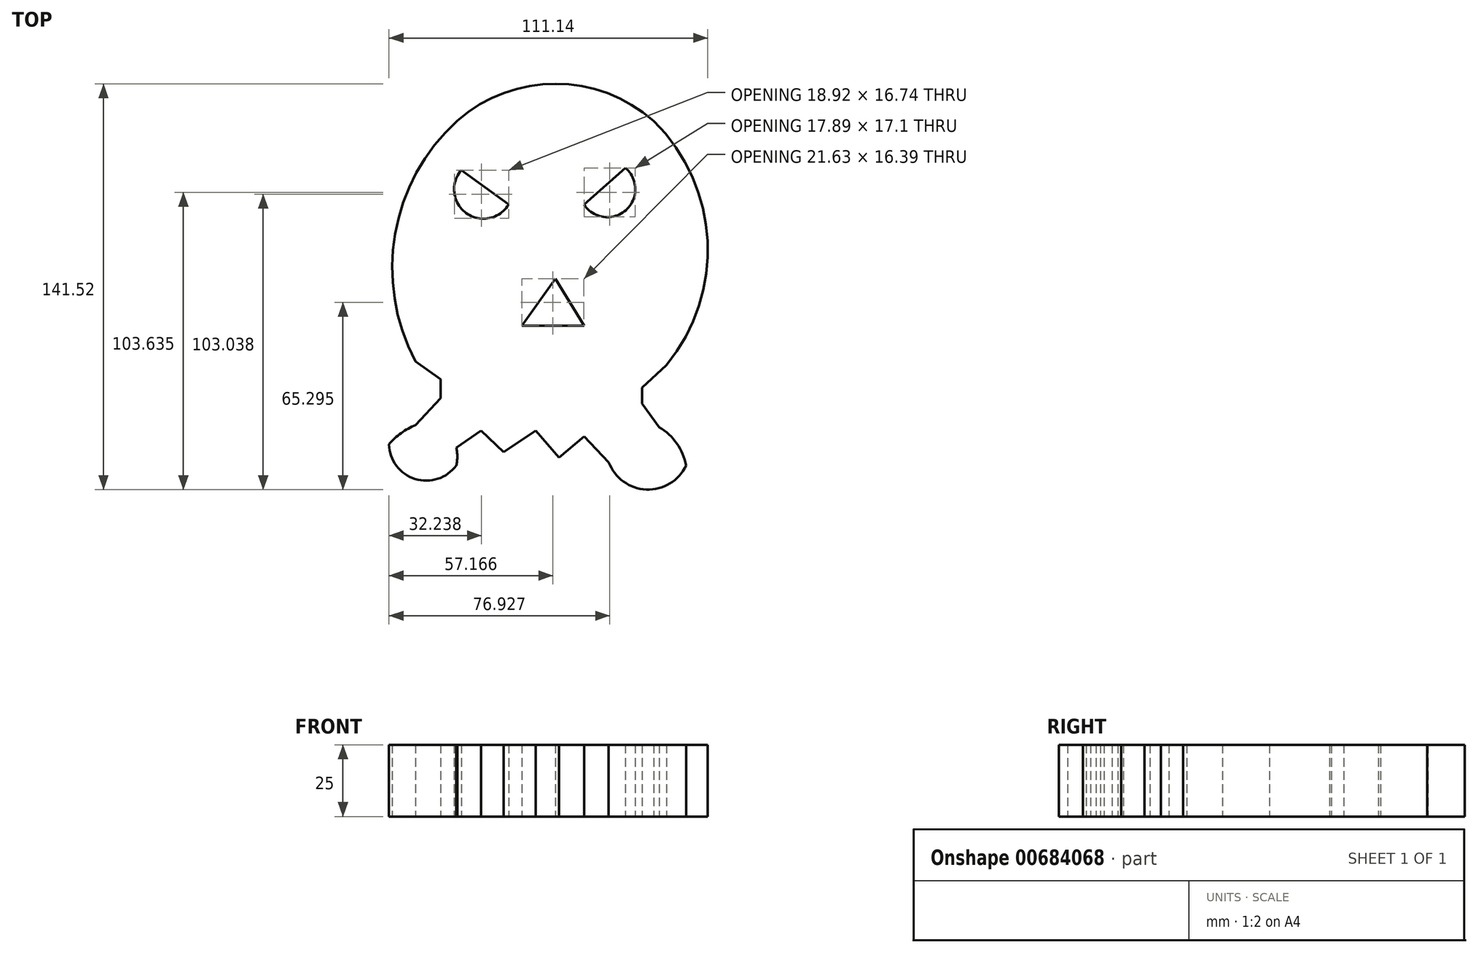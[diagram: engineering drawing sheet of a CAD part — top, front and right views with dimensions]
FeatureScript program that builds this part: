
annotation { "Feature Type Name" : "Feature", "Feature Type Description" : "" }
export const myFeature = defineFeature(function(context is Context, id is Id, definition is map)
    precondition{}
    {
        {
            var Q0;
            Q0=qCreatedBy(makeId("Top.planeOp"),FACE);
            var sketch = newSketch(context, id + "F0", { "sketchPlane" : qUnion([Q0])});
            skArc(sketch, "E0", {"start": v(-67.98, -57.7) * mm, "mid": v(-58.88, -69.78) * mm, "end": v(-44.52, -65.08) * mm});
            skArc(sketch, "E1", {"start": v(8.63, -63.91) * mm, "mid": v(21.72, -73.47) * mm, "end": v(35.6, -65.08) * mm});
            skArc(sketch, "E2", {"start": v(-44.52, -65.08) * mm, "mid": v(-48.16, -59.07) * mm, "end": v(-54.99, -57.38) * mm});
            skArc(sketch, "E3", {"start": v(-54.99, -57.38) * mm, "mid": v(-61.53, -55.67) * mm, "end": v(-67.98, -57.7) * mm});
            skArc(sketch, "E4", {"start": v(22.36, -58.86) * mm, "mid": v(14.9, -59.76) * mm, "end": v(8.63, -63.91) * mm});
            skArc(sketch, "E5", {"start": v(35.6, -65.08) * mm, "mid": v(29.71, -60.4) * mm, "end": v(22.36, -58.86) * mm});
            skArc(sketch, "E6", {"start": v(-52.7, -49.36) * mm, "mid": v(-61.1, -52.13) * mm, "end": v(-67.98, -57.7) * mm});
            skArc(sketch, "E7", {"start": v(-44.52, -65.08) * mm, "mid": v(-45.7, -55.7) * mm, "end": v(-52.7, -49.36) * mm});
            skArc(sketch, "E8", {"start": v(20.24, -49.36) * mm, "mid": v(11.74, -54.5) * mm, "end": v(8.63, -63.91) * mm});
            skArc(sketch, "E9", {"start": v(35.6, -65.08) * mm, "mid": v(30.29, -54.9) * mm, "end": v(20.24, -49.36) * mm});
            skLineSegment(sketch, "E10", {"start": v(-44.52, -58.88) * mm, "end": v(-35.82, -52.86) * mm});
            skLineSegment(sketch, "E11", {"start": v(-35.82, -52.86) * mm, "end": v(-28.06, -60.42) * mm});
            skLineSegment(sketch, "E12", {"start": v(-28.06, -60.42) * mm, "end": v(-16.8, -52.86) * mm});
            skLineSegment(sketch, "E13", {"start": v(-16.8, -52.86) * mm, "end": v(-8.66, -62.36) * mm});
            skLineSegment(sketch, "E14", {"start": v(-8.66, -62.36) * mm, "end": v(0, -54.94) * mm});
            skLineSegment(sketch, "E15", {"start": v(0, -54.94) * mm, "end": v(8.63, -63.91) * mm});
            skLineSegment(sketch, "E16", {"start": v(-58.7, -50.98) * mm, "end": v(-49.98, -41.6) * mm});
            skLineSegment(sketch, "E17", {"start": v(-49.98, -41.6) * mm, "end": v(-49.98, -35.01) * mm});
            skLineSegment(sketch, "E18", {"start": v(-49.98, -35.01) * mm, "end": v(-58.7, -28.8) * mm});
            skLineSegment(sketch, "E19", {"start": v(26.28, -51.74) * mm, "end": v(20.24, -43.55) * mm});
            skLineSegment(sketch, "E20", {"start": v(20.24, -43.55) * mm, "end": v(20.24, -37.92) * mm});
            skLineSegment(sketch, "E21", {"start": v(20.24, -37.92) * mm, "end": v(28.73, -30.08) * mm});
            skArc(sketch, "E22", {"start": v(-44.13, 55.18) * mm, "mid": v(-65.82, 15.7) * mm, "end": v(-58.7, -28.8) * mm});
            skArc(sketch, "E23", {"start": v(28.73, -30.08) * mm, "mid": v(43.07, 13.3) * mm, "end": v(24.34, 54.99) * mm});
            skArc(sketch, "E24", {"start": v(24.34, 54.99) * mm, "mid": v(-9.86, 68.03) * mm, "end": v(-44.13, 55.18) * mm});
            skLineSegment(sketch, "E25", {"start": v(-21.63, -16.4) * mm, "end": v(0, -16.4) * mm});
            skLineSegment(sketch, "E26", {"start": v(0, -16.4) * mm, "end": v(-9.99, 0) * mm});
            skLineSegment(sketch, "E27", {"start": v(-21.63, -16.4) * mm, "end": v(-9.99, 0) * mm});
            skLineSegment(sketch, "E28", {"start": v(-42.77, 37.92) * mm, "end": v(-26.28, 25.9) * mm});
            skLineSegment(sketch, "E29", {"start": v(0, 25.9) * mm, "end": v(14.45, 38.7) * mm});
            skArc(sketch, "E30", {"start": v(-42.77, 37.92) * mm, "mid": v(-41.06, 22.94) * mm, "end": v(-26.28, 25.9) * mm});
            skArc(sketch, "E31", {"start": v(0, 25.9) * mm, "mid": v(14.6, 23.96) * mm, "end": v(14.45, 38.7) * mm});
            skSolve(sketch);
        }
        {
            var Q0;
            {var subQ3=sQuery(id+"F0.wireOp",EDGE,"E8");Q0=makeQuery(id+"F0.imprint","IMPRINT",FACE,{"disambiguationData":[TD([[makeQuery(id+"F0.imprint","IMPRINT",EDGE,{"derivedFrom":subQ3}),-1.0]])]});}
            extrude(context, id + "F1", {"entities" : qUnion([Q0]), "depth" : 8 * mm, "offsetDistance" : 25 * mm});
        }
        {
            var Q0;
            Q0 = qSketchRegion(id + "F0", true);
            extrude(context, id + "F2", {"entities" : qUnion([Q0]), "operationType" : NewBodyOperationType.ADD, "depth" : 25 * mm, "offsetDistance" : 25 * mm});
        }
    });
